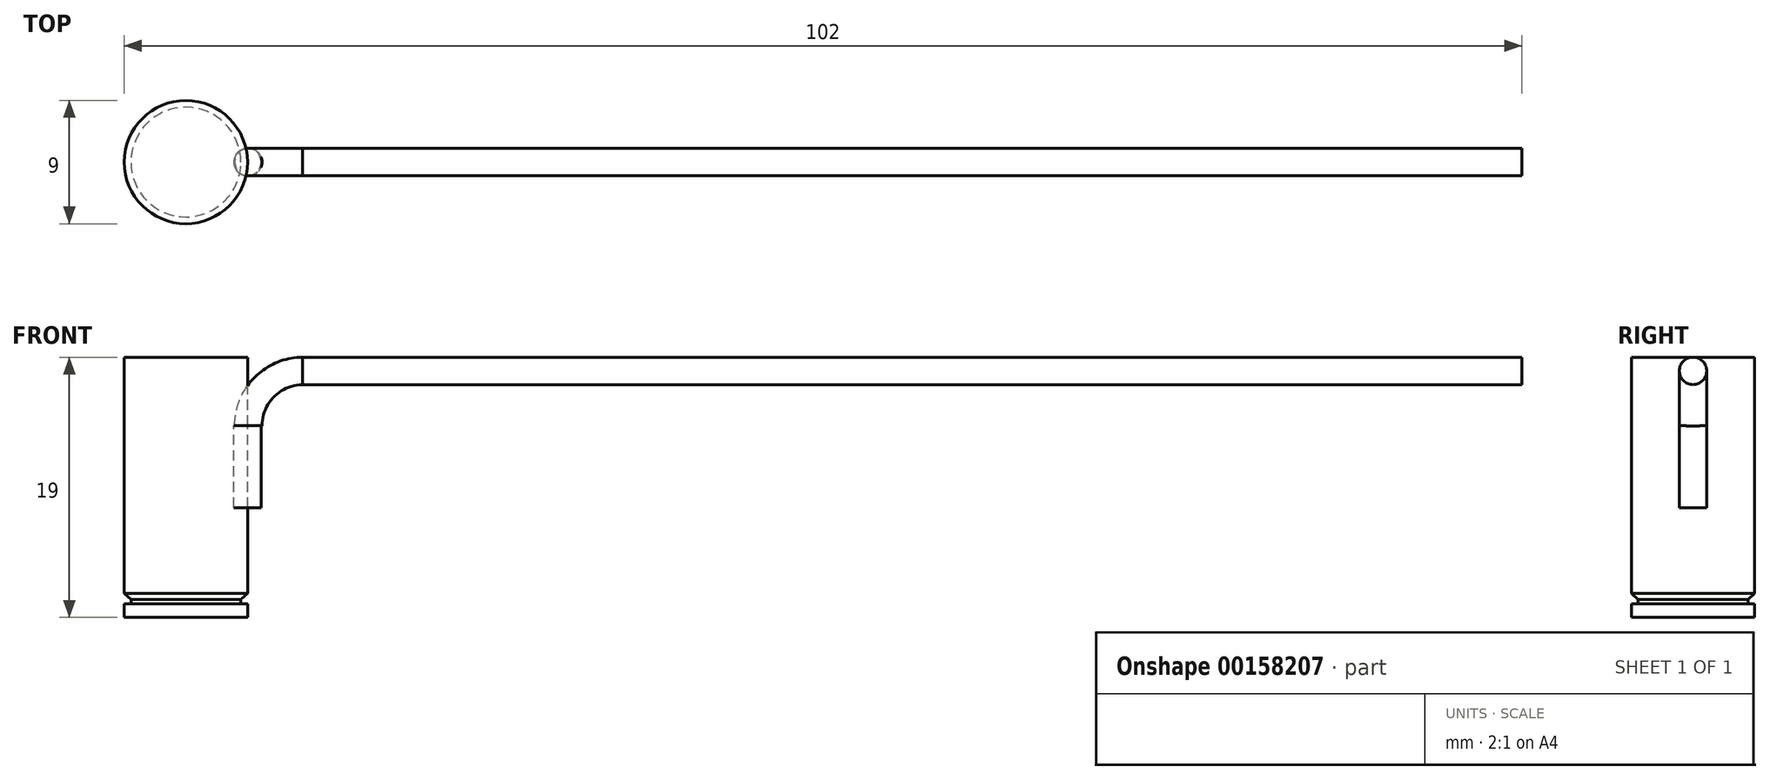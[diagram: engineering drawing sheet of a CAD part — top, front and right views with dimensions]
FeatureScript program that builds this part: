
annotation { "Feature Type Name" : "Feature", "Feature Type Description" : "" }
export const myFeature = defineFeature(function(context is Context, id is Id, definition is map)
    precondition{}
    {
        {
            var Q0;
            Q0=qCreatedBy(makeId("Top.planeOp"),FACE);
            var sketch = newSketch(context, id + "F0", { "sketchPlane" : qUnion([Q0])});
            skCircle(sketch, "E0", {"center": v(0, 0) * mm, "radius": 1 * mm});
            skSolve(sketch);
        }
        {
            var Q0;
            Q0=qCreatedBy(makeId("Right.planeOp"),FACE);
            cPlane(context, id + "F1", {"entities" : qUnion([Q0]), "cplaneType" : CPlaneType.OFFSET, "offset" : 4 * mm, "width" : 150 * mm, "height" : 150 * mm});
        }
        {
            var Q0;
            Q0=qCreatedBy(id+"F1.planeOp",FACE);
            var sketch = newSketch(context, id + "F2", { "sketchPlane" : qUnion([Q0])});
            skCircle(sketch, "E1", {"center": v(0, 4) * mm, "radius": 1 * mm});
            skSolve(sketch);
        }
        {
            var Q0;
            Q0 = qSketchRegion(id + "F0", true);
            extrude(context, id + "F3", {"entities" : qUnion([Q0]), "oppositeDirection" : true, "depth" : 6 * mm});
        }
        {
            var Q0;
            Q0 = qSketchRegion(id + "F2", true);
            extrude(context, id + "F4", {"entities" : qUnion([Q0]), "depth" : 89 * mm});
        }
        {
            var Q0;
            Q0=qCreatedBy(makeId("Front.planeOp"),FACE);
            var sketch = newSketch(context, id + "F5", { "sketchPlane" : qUnion([Q0])});
            skArc(sketch, "E2", {"start": v(0, 0) * mm, "mid": v(1.17, 2.85) * mm, "end": v(4, 4.06) * mm});
            skSolve(sketch);
        }
        {
            var Q0;
            Q0=makeQuery(id+"F4.opExtrude","CAP_FACE",FACE,{"disambiguationData":[OSD([sQuery(id+"F2.wireOp",EDGE,"E1")])],"isStart":true});
            var Q1;
            Q1=sQuery(id+"F5.wireOp",EDGE,"E2");
            sweep(context, id + "F6", {"profiles" : qUnion([Q0]), "path" : qUnion([Q1])});
        }
        {
            var Q0;
            Q0=qCreatedBy(makeId("Top.planeOp"),FACE);
            cPlane(context, id + "F7", {"entities" : qUnion([Q0]), "cplaneType" : CPlaneType.OFFSET, "offset" : 5 * mm, "width" : 150 * mm, "height" : 150 * mm});
        }
        {
            var Q0;
            Q0=qCreatedBy(id+"F7.planeOp",FACE);
            var sketch = newSketch(context, id + "F8", { "sketchPlane" : qUnion([Q0])});
            skLineSegment(sketch, "E3", {"start": v(0, 0) * mm, "end": v(-4.5, 0) * mm});
            skLineSegment(sketch, "E4", {"start": v(-4.5, 0) * mm, "end": v(-9, 0) * mm});
            skCircle(sketch, "E5", {"center": v(-4.5, 0) * mm, "radius": 4.5 * mm});
            skSolve(sketch);
        }
        {
            var Q0;
            {var subQ0=sQuery(id+"F8.wireOp",EDGE,"E3");Q0=makeQuery(id+"F8.imprint","IMPRINT",FACE,{"disambiguationData":[TD([[makeQuery(id+"F8.imprint","IMPRINT",EDGE,{"derivedFrom":subQ0}),1.0]])]});}
            var Q1;
            {var subQ0=sQuery(id+"F8.wireOp",EDGE,"E3");Q1=makeQuery(id+"F8.imprint","IMPRINT",FACE,{"disambiguationData":[TD([[makeQuery(id+"F8.imprint","IMPRINT",EDGE,{"derivedFrom":subQ0}),-1.0]])]});}
            extrude(context, id + "F9", {"entities" : qUnion([Q0, Q1]), "oppositeDirection" : true, "depth" : 19 * mm});
        }
        {
            var Q0;
            Q0=qCreatedBy(makeId("Front.planeOp"),FACE);
            var sketch = newSketch(context, id + "F10", { "sketchPlane" : qUnion([Q0])});
            skLineSegment(sketch, "E6", {"start": v(0, -14.01) * mm, "end": v(0, -13) * mm});
            skLineSegment(sketch, "E7", {"start": v(0, -13) * mm, "end": v(-0.5, -13) * mm});
            skLineSegment(sketch, "E8", {"start": v(1.13, -12.53) * mm, "end": v(1.13, -13.99) * mm});
            skLineSegment(sketch, "E9", {"start": v(1.13, -13.99) * mm, "end": v(0, -14.01) * mm});
            skLineSegment(sketch, "E10", {"start": v(-0.5, -13) * mm, "end": v(-0.5, -12.7) * mm});
            skLineSegment(sketch, "E11", {"start": v(-0.5, -12.7) * mm, "end": v(0, -12.25) * mm});
            skLineSegment(sketch, "E12", {"start": v(0, -12.25) * mm, "end": v(1.13, -12.53) * mm});
            skSolve(sketch);
        }
        {
            var Q0;
            Q0=qCreatedBy(makeId("Front.planeOp"),FACE);
            var sketch = newSketch(context, id + "F11", { "sketchPlane" : qUnion([Q0])});
            skLineSegment(sketch, "E13", {"start": v(-4.5, -13.96) * mm, "end": v(-4.5, -11.93) * mm});
            skSolve(sketch);
        }
        {
            var Q0;
            Q0=makeQuery(id+"F10.imprint","IMPRINT",FACE,{"disambiguationData":[TD([[makeQuery(id+"F10.imprint","IMPRINT",EDGE,{"derivedFrom":sQuery(id+"F10.wireOp",EDGE,"E6")}),-1.0]])]});
            var Q1;
            Q1=sQuery(id+"F11.wireOp",EDGE,"E13");
            revolve(context, id + "F12", {"operationType" : NewBodyOperationType.REMOVE, "entities" : qUnion([Q0]), "axis" : qUnion([Q1]), "revolveType" : RevolveType.FULL, "oppositeDirection" : true});
        }
    });
